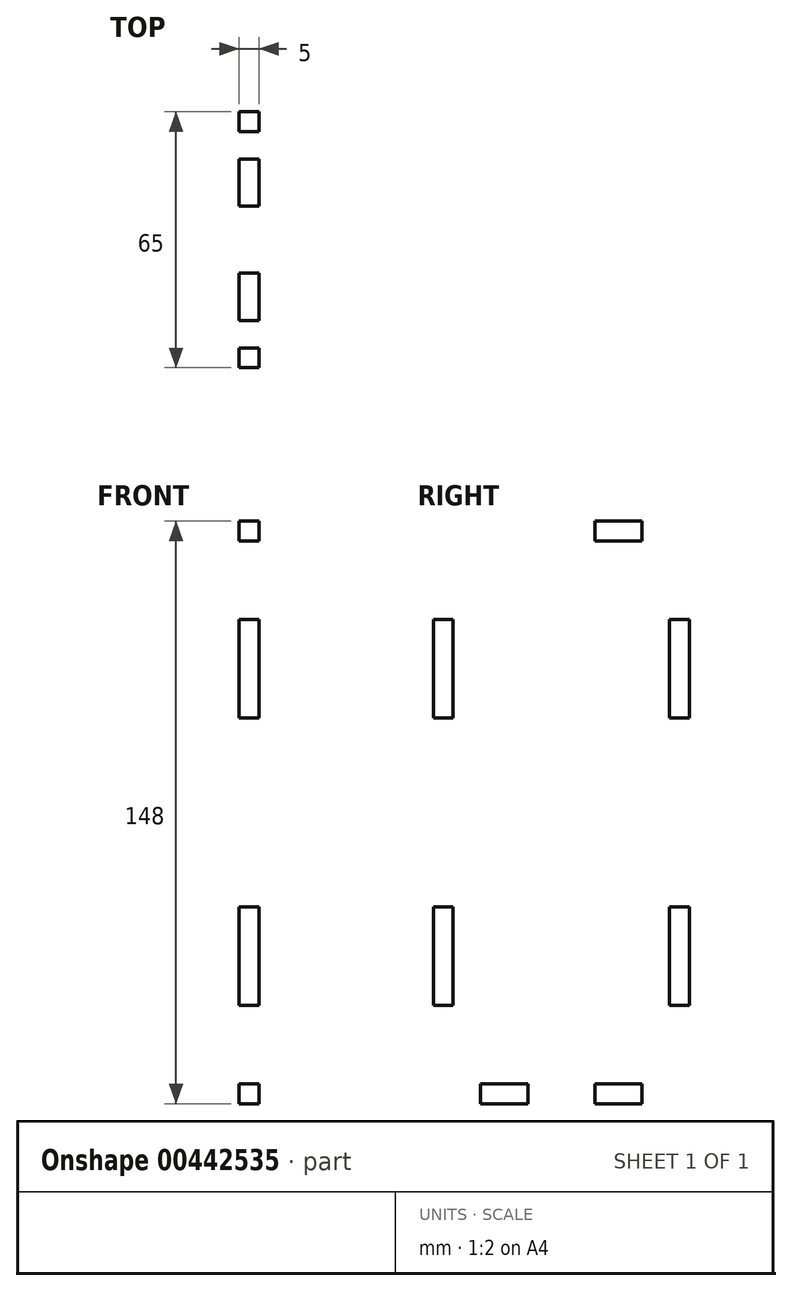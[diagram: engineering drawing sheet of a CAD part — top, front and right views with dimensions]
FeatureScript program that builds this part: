
annotation { "Feature Type Name" : "Feature", "Feature Type Description" : "" }
export const myFeature = defineFeature(function(context is Context, id is Id, definition is map)
    precondition{}
    {
        {
            var Q0;
            Q0=qCreatedBy(makeId("Right.planeOp"),FACE);
            var sketch = newSketch(context, id + "F0", { "sketchPlane" : qUnion([Q0])});
            skLineSegment(sketch, "E0.bottom", {"start": v(27.5, 69) * mm, "end": v(-27.5, 69) * mm});
            skLineSegment(sketch, "E0.top", {"start": v(27.5, -69) * mm, "end": v(-27.5, -69) * mm});
            skLineSegment(sketch, "E0.left", {"start": v(27.5, 69) * mm, "end": v(27.5, -69) * mm});
            skLineSegment(sketch, "E0.right", {"start": v(-27.5, 69) * mm, "end": v(-27.5, -69) * mm});
            skPoint(sketch, "E0.middle", {"position": v(0, 0) * mm});
            skLineSegment(sketch, "E1.bottom", {"start": v(-20.5, 69) * mm, "end": v(-8.5, 69) * mm});
            skLineSegment(sketch, "E1.top", {"start": v(-20.5, 74) * mm, "end": v(-8.5, 74) * mm});
            skLineSegment(sketch, "E1.left", {"start": v(-20.5, 69) * mm, "end": v(-20.5, 74) * mm});
            skLineSegment(sketch, "E1.right", {"start": v(-8.5, 69) * mm, "end": v(-8.5, 74) * mm});
            skLineSegment(sketch, "E2", {"start": v(0, 0) * mm, "end": v(0, 69) * mm, "construction": true});
            skLineSegment(sketch, "E3.bottom", {"start": v(-27.5, 49) * mm, "end": v(-32.5, 49) * mm});
            skLineSegment(sketch, "E3.top", {"start": v(-27.5, 24) * mm, "end": v(-32.5, 24) * mm});
            skLineSegment(sketch, "E3.left", {"start": v(-27.5, 49) * mm, "end": v(-27.5, 24) * mm});
            skLineSegment(sketch, "E3.right", {"start": v(-32.5, 49) * mm, "end": v(-32.5, 24) * mm});
            skLineSegment(sketch, "E4", {"start": v(-27.5, 0) * mm, "end": v(27.5, 0) * mm, "construction": true});
            skLineSegment(sketch, "E5.MirrorCS", {"start": v(-32.5, -49) * mm, "end": v(-32.5, -24) * mm});
            skLineSegment(sketch, "E6.MirrorCS", {"start": v(-27.5, -49) * mm, "end": v(-32.5, -49) * mm});
            skLineSegment(sketch, "E7.MirrorCS", {"start": v(-27.5, -24) * mm, "end": v(-32.5, -24) * mm});
            skLineSegment(sketch, "E8.MirrorCS", {"start": v(-20.5, -69) * mm, "end": v(-20.5, -74) * mm});
            skLineSegment(sketch, "E9.MirrorCS", {"start": v(-8.5, -69) * mm, "end": v(-8.5, -74) * mm});
            skLineSegment(sketch, "E10.MirrorCS", {"start": v(-20.5, -74) * mm, "end": v(-8.5, -74) * mm});
            skLineSegment(sketch, "E11.MirrorCS", {"start": v(8.5, 69) * mm, "end": v(8.5, 74) * mm});
            skLineSegment(sketch, "E12.MirrorCS", {"start": v(20.5, 74) * mm, "end": v(8.5, 74) * mm});
            skLineSegment(sketch, "E13.MirrorCS", {"start": v(20.5, 69) * mm, "end": v(20.5, 74) * mm});
            skLineSegment(sketch, "E14.MirrorCS", {"start": v(27.5, 49) * mm, "end": v(32.5, 49) * mm});
            skLineSegment(sketch, "E15.MirrorCS", {"start": v(32.5, 49) * mm, "end": v(32.5, 24) * mm});
            skLineSegment(sketch, "E16.MirrorCS", {"start": v(27.5, 24) * mm, "end": v(32.5, 24) * mm});
            skLineSegment(sketch, "E17.MirrorCS", {"start": v(27.5, -24) * mm, "end": v(32.5, -24) * mm});
            skLineSegment(sketch, "E18.MirrorCS", {"start": v(32.5, -49) * mm, "end": v(32.5, -24) * mm});
            skLineSegment(sketch, "E19.MirrorCS", {"start": v(27.5, -49) * mm, "end": v(32.5, -49) * mm});
            skLineSegment(sketch, "E20.MirrorCS", {"start": v(20.5, -74) * mm, "end": v(8.5, -74) * mm});
            skLineSegment(sketch, "E21.MirrorCS", {"start": v(20.5, -69) * mm, "end": v(20.5, -74) * mm});
            skLineSegment(sketch, "E22.MirrorCS", {"start": v(8.5, -69) * mm, "end": v(8.5, -74) * mm});
            skSolve(sketch);
        }
        {
            var Q0;
            {var subQ15=sQuery(id+"F0.wireOp",EDGE,"E1.bottom");Q0=makeQuery(id+"F0.imprint","IMPRINT",FACE,{"disambiguationData":[TD([[makeQuery(id+"F0.imprint","IMPRINT",EDGE,{"derivedFrom":subQ15}),-1.0]])]});}
            var Q1;
            Q1=makeQuery(id+"F0.imprint","IMPRINT",FACE,{"disambiguationData":[TD([[makeQuery(id+"F0.imprint","IMPRINT",EDGE,{"derivedFrom":sQuery(id+"F0.wireOp",EDGE,"E1.bottom")}),1.0]])]});
            var Q2;
            {var subQ0=sQuery(id+"F0.wireOp",EDGE,"E11.MirrorCS");Q2=makeQuery(id+"F0.imprint","IMPRINT",FACE,{"disambiguationData":[TD([[makeQuery(id+"F0.imprint","IMPRINT",EDGE,{"derivedFrom":subQ0}),-1.0]])]});}
            var Q3;
            {var subQ0=sQuery(id+"F0.wireOp",EDGE,"E14.MirrorCS");Q3=makeQuery(id+"F0.imprint","IMPRINT",FACE,{"disambiguationData":[TD([[makeQuery(id+"F0.imprint","IMPRINT",EDGE,{"derivedFrom":subQ0}),-1.0]])]});}
            var Q4;
            {var subQ0=sQuery(id+"F0.wireOp",EDGE,"E17.MirrorCS");Q4=makeQuery(id+"F0.imprint","IMPRINT",FACE,{"disambiguationData":[TD([[makeQuery(id+"F0.imprint","IMPRINT",EDGE,{"derivedFrom":subQ0}),-1.0]])]});}
            var Q5;
            Q5=makeQuery(id+"F0.imprint","IMPRINT",FACE,{"disambiguationData":[TD([[makeQuery(id+"F0.imprint","IMPRINT",EDGE,{"derivedFrom":sQuery(id+"F0.wireOp",EDGE,"E20.MirrorCS")}),-1.0]])]});
            var Q6;
            {var subQ0=sQuery(id+"F0.wireOp",EDGE,"E8.MirrorCS");Q6=makeQuery(id+"F0.imprint","IMPRINT",FACE,{"disambiguationData":[TD([[makeQuery(id+"F0.imprint","IMPRINT",EDGE,{"derivedFrom":subQ0}),1.0]])]});}
            var Q7;
            Q7=makeQuery(id+"F0.imprint","IMPRINT",FACE,{"disambiguationData":[TD([[makeQuery(id+"F0.imprint","IMPRINT",EDGE,{"derivedFrom":sQuery(id+"F0.wireOp",EDGE,"E5.MirrorCS")}),-1.0]])]});
            var Q8;
            Q8=makeQuery(id+"F0.imprint","IMPRINT",FACE,{"disambiguationData":[TD([[makeQuery(id+"F0.imprint","IMPRINT",EDGE,{"derivedFrom":sQuery(id+"F0.wireOp",EDGE,"E3.bottom")}),1.0]])]});
            extrude(context, id + "F1", {"entities" : qUnion([Q0, Q1, Q2, Q3, Q4, Q5, Q6, Q7, Q8]), "depth" : 5 * mm});
        }
    });
